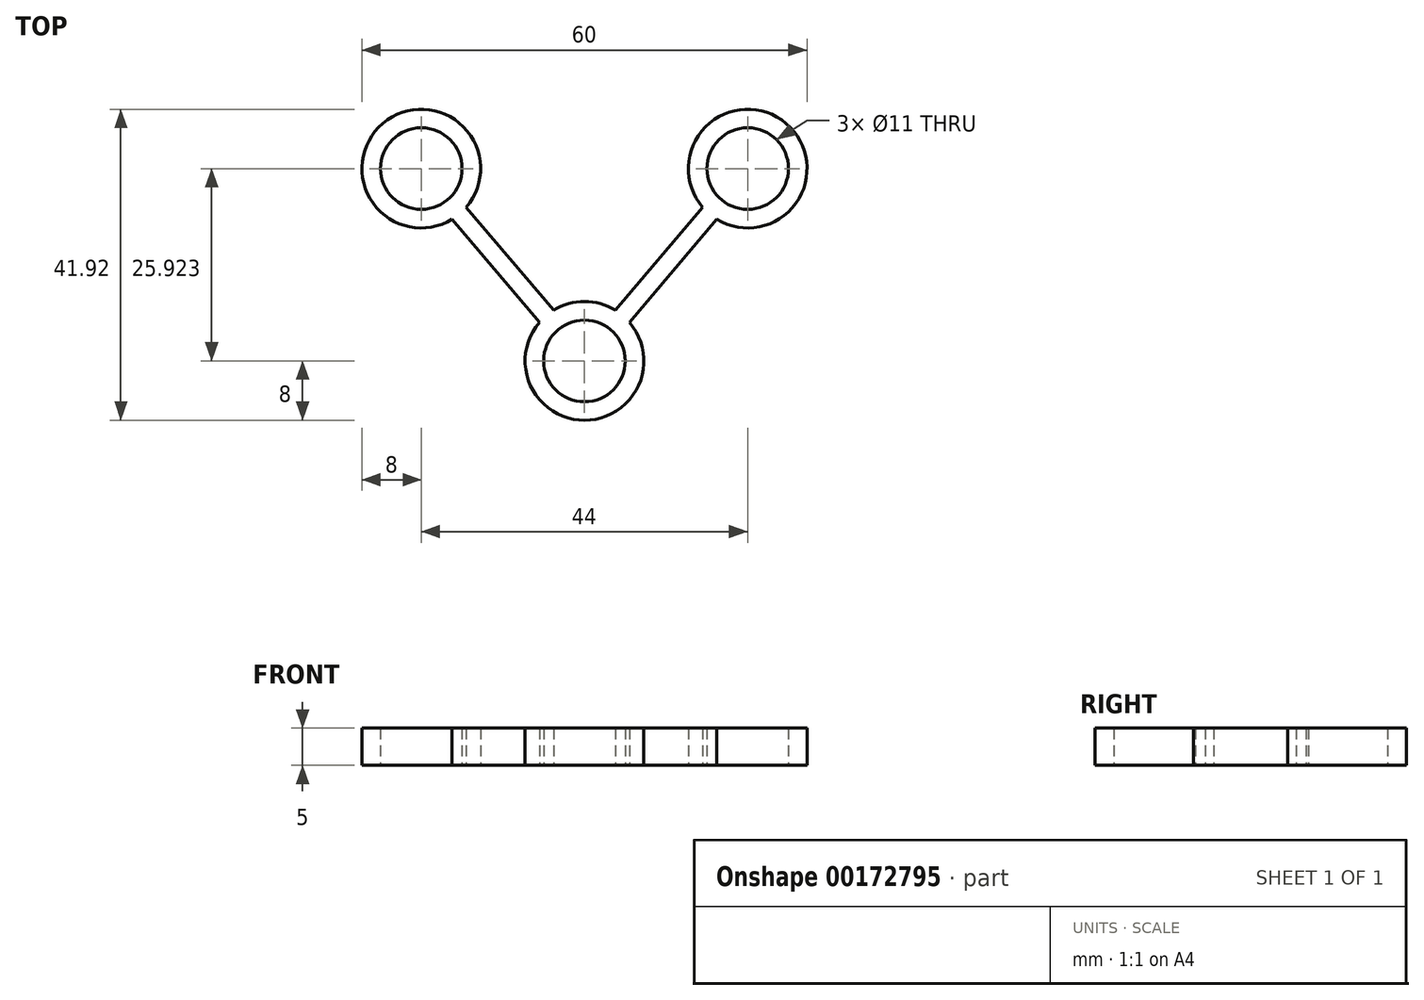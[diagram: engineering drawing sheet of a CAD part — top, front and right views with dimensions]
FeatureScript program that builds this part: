
annotation { "Feature Type Name" : "Feature", "Feature Type Description" : "" }
export const myFeature = defineFeature(function(context is Context, id is Id, definition is map)
    precondition{}
    {
        {
            var Q0;
            Q0=qCreatedBy(makeId("Top.planeOp"),FACE);
            var sketch = newSketch(context, id + "F0", { "sketchPlane" : qUnion([Q0])});
            skCircle(sketch, "E0", {"center": v(0, 0) * mm, "radius": 5.5 * mm});
            skArc(sketch, "E1", {"start": v(-6.07, 5.22) * mm, "mid": v(0, -8) * mm, "end": v(6.07, 5.22) * mm});
            skCircle(sketch, "E2", {"center": v(-22, 25.92) * mm, "radius": 5.5 * mm});
            skCircle(sketch, "E3", {"center": v(22, 25.92) * mm, "radius": 5.5 * mm});
            skArc(sketch, "E4", {"start": v(-15.93, 20.7) * mm, "mid": v(-27.18, 32.02) * mm, "end": v(-17.84, 19.09) * mm});
            skArc(sketch, "E5", {"start": v(17.84, 19.09) * mm, "mid": v(27.18, 32.02) * mm, "end": v(15.93, 20.7) * mm});
            skLineSegment(sketch, "E6", {"start": v(-22, 25.92) * mm, "end": v(0, 0) * mm, "construction": true});
            skLineSegment(sketch, "E7", {"start": v(22, 25.92) * mm, "end": v(0, 0) * mm, "construction": true});
            skLineSegment(sketch, "E8.0", {"start": v(-17.84, 19.09) * mm, "end": v(-6.07, 5.22) * mm});
            skLineSegment(sketch, "E9.0", {"start": v(-15.93, 20.7) * mm, "end": v(-4.16, 6.83) * mm});
            skLineSegment(sketch, "E10.0", {"start": v(15.93, 20.7) * mm, "end": v(4.16, 6.83) * mm});
            skLineSegment(sketch, "E11.0", {"start": v(17.84, 19.09) * mm, "end": v(6.07, 5.22) * mm});
            skArc(sketch, "E12.trimOffspring", {"start": v(4.16, 6.83) * mm, "mid": v(0, 8) * mm, "end": v(-4.16, 6.83) * mm});
            skSolve(sketch);
        }
        {
            var Q0;
            Q0 = qSketchRegion(id + "F0", true);
            extrude(context, id + "F1", {"entities" : qUnion([Q0]), "depth" : 5 * mm});
        }
    });
